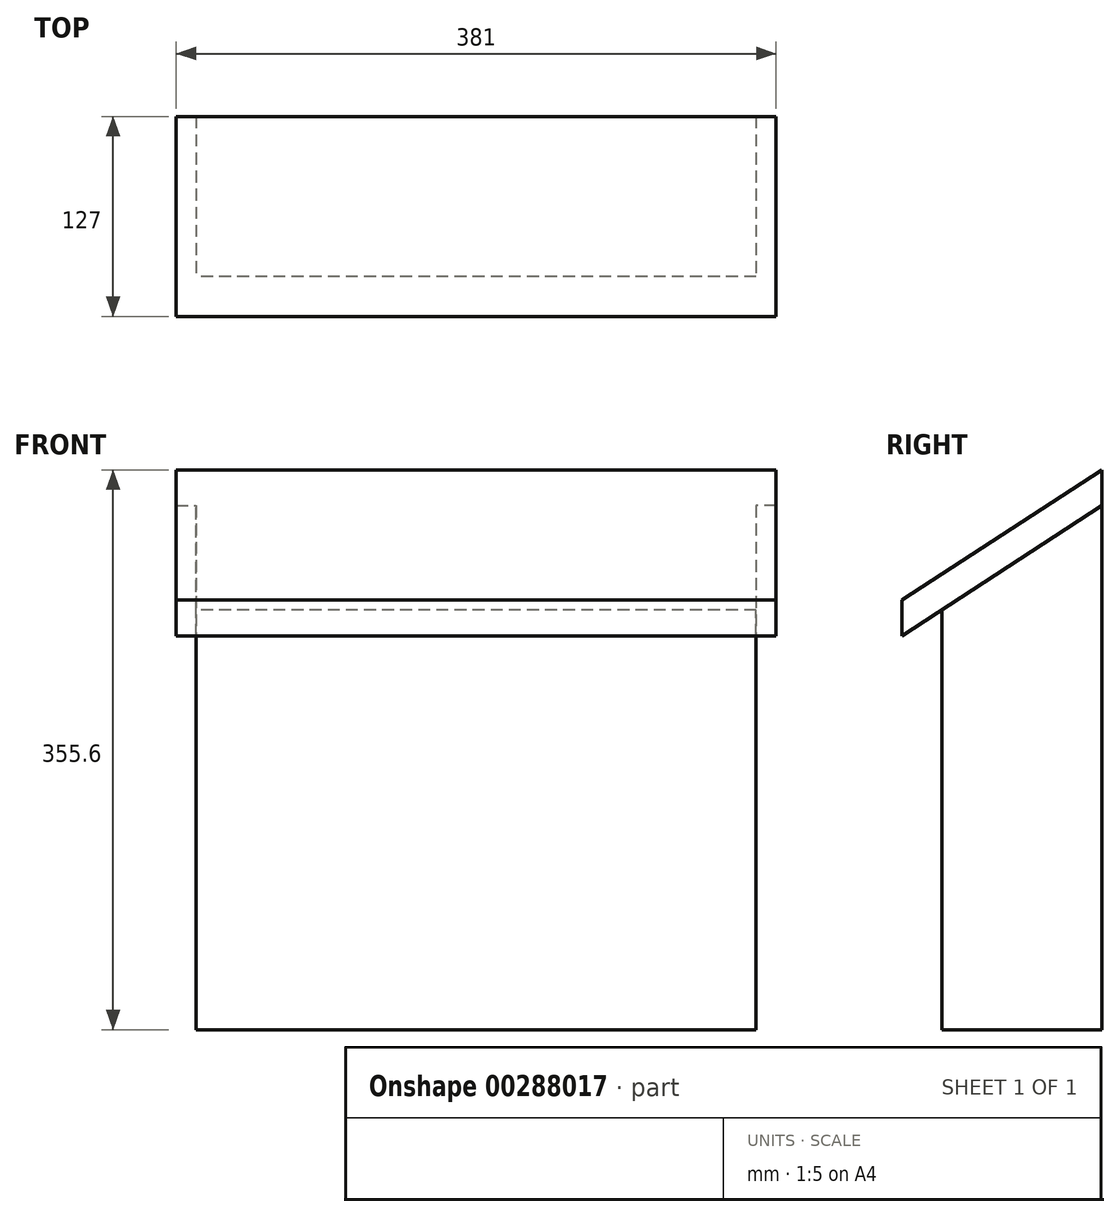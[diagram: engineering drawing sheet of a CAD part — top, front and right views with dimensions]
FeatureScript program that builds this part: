
annotation { "Feature Type Name" : "Feature", "Feature Type Description" : "" }
export const myFeature = defineFeature(function(context is Context, id is Id, definition is map)
    precondition{}
    {
        {
            var Q0;
            Q0=qCreatedBy(makeId("Right.planeOp"),FACE);
            var sketch = newSketch(context, id + "F0", { "sketchPlane" : qUnion([Q0])});
            skLineSegment(sketch, "E0", {"start": v(0, 0) * mm, "end": v(0, 266.65) * mm});
            skLineSegment(sketch, "E1", {"start": v(0, 266.65) * mm, "end": v(-25.4, 250.1) * mm});
            skLineSegment(sketch, "E2", {"start": v(-25.4, 250.1) * mm, "end": v(-25.4, 272.84) * mm});
            skLineSegment(sketch, "E3", {"start": v(-25.4, 272.84) * mm, "end": v(101.6, 355.6) * mm});
            skLineSegment(sketch, "E4", {"start": v(101.6, 355.6) * mm, "end": v(101.6, 0) * mm});
            skLineSegment(sketch, "E5", {"start": v(101.6, 0) * mm, "end": v(0, 0) * mm});
            skSolve(sketch);
        }
        {
            var Q0;
            Q0 = qSketchRegion(id + "F0", true);
            extrude(context, id + "F1", {"entities" : qUnion([Q0]), "depth" : 355.6 * mm});
        }
        {
            var Q0;
            Q0=makeQuery(id+"F1.opExtrude","CAP_FACE",FACE,{"disambiguationData":[OSD([sQuery(id+"F0.wireOp",EDGE,"E0"),sQuery(id+"F0.wireOp",EDGE,"E1"),sQuery(id+"F0.wireOp",EDGE,"E2"),sQuery(id+"F0.wireOp",EDGE,"E3"),sQuery(id+"F0.wireOp",EDGE,"E4"),sQuery(id+"F0.wireOp",EDGE,"E5")])],"isStart":false});
            var sketch = newSketch(context, id + "F2", { "sketchPlane" : qUnion([Q0])});
            skLineSegment(sketch, "E6", {"start": v(0, 266.65) * mm, "end": v(101.6, 332.86) * mm});
            skSolve(sketch);
        }
        {
            var Q0;
            {var subQ1=sQuery(id+"F2.wireOp",EDGE,"E6");Q0=makeQuery(id+"F2.imprint","IMPRINT",FACE,{"disambiguationData":[TD([[makeQuery(id+"F2.imprint","IMPRINT",EDGE,{"derivedFrom":subQ1}),1.0]])]});}
            extrude(context, id + "F3", {"entities" : qUnion([Q0]), "operationType" : NewBodyOperationType.ADD, "depth" : 12.7 * mm});
        }
        {
            var Q0;
            Q0=makeQuery(id+"F1.opExtrude","CAP_FACE",FACE,{"disambiguationData":[OSD([sQuery(id+"F0.wireOp",EDGE,"E0"),sQuery(id+"F0.wireOp",EDGE,"E1"),sQuery(id+"F0.wireOp",EDGE,"E2"),sQuery(id+"F0.wireOp",EDGE,"E3"),sQuery(id+"F0.wireOp",EDGE,"E4"),sQuery(id+"F0.wireOp",EDGE,"E5")])],"isStart":true});
            var sketch = newSketch(context, id + "F4", { "sketchPlane" : qUnion([Q0])});
            skLineSegment(sketch, "E7", {"start": v(0, 266.65) * mm, "end": v(-101.6, 332.86) * mm});
            skSolve(sketch);
        }
        {
            var Q0;
            {var subQ1=sQuery(id+"F4.wireOp",EDGE,"E7");Q0=makeQuery(id+"F4.imprint","IMPRINT",FACE,{"disambiguationData":[TD([[makeQuery(id+"F4.imprint","IMPRINT",EDGE,{"derivedFrom":subQ1}),-1.0]])]});}
            extrude(context, id + "F5", {"entities" : qUnion([Q0]), "operationType" : NewBodyOperationType.ADD, "depth" : 12.7 * mm});
        }
    });
